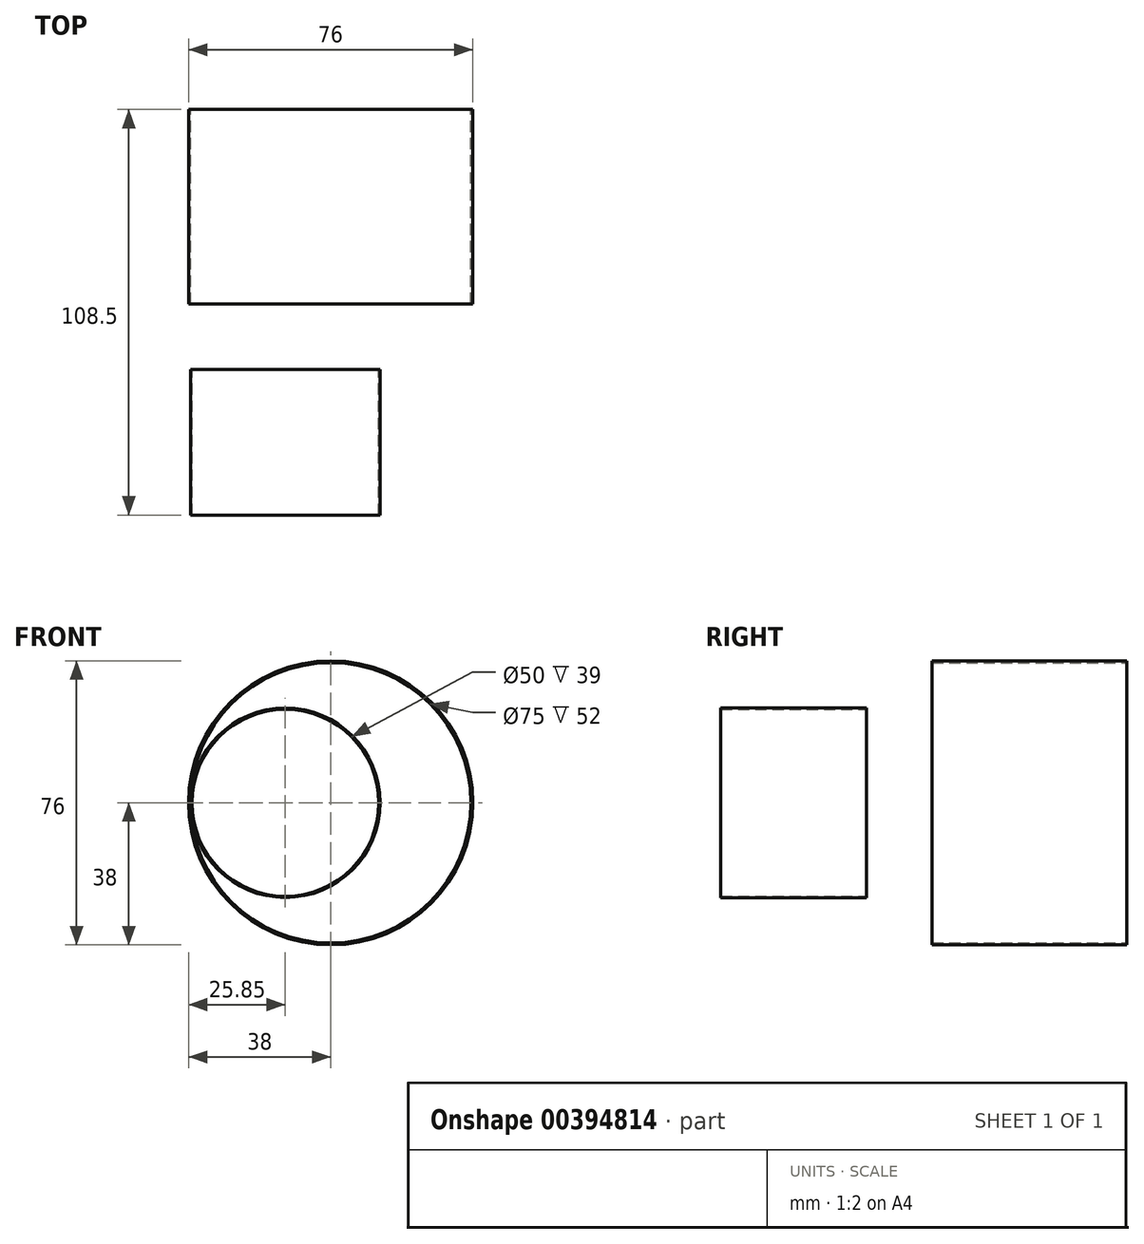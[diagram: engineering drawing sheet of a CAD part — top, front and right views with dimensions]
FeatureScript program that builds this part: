
annotation { "Feature Type Name" : "Feature", "Feature Type Description" : "" }
export const myFeature = defineFeature(function(context is Context, id is Id, definition is map)
    precondition{}
    {
        {
            var Q0;
            Q0=qCreatedBy(makeId("Front.planeOp"),FACE);
            var sketch = newSketch(context, id + "F0", { "sketchPlane" : qUnion([Q0])});
            skCircle(sketch, "E0", {"center": v(0, 0) * mm, "radius": 38 * mm});
            skCircle(sketch, "E1", {"center": v(0, 0) * mm, "radius": 37.5 * mm});
            skSolve(sketch);
        }
        {
            var Q0;
            Q0=makeQuery(id+"F0.imprint","IMPRINT",FACE,{"disambiguationData":[TD([[makeQuery(id+"F0.imprint","IMPRINT",EDGE,{"derivedFrom":sQuery(id+"F0.wireOp",EDGE,"E0")}),1.0]])]});
            extrude(context, id + "F1", {"entities" : qUnion([Q0]), "depth" : 52 * mm});
        }
        {
            var Q0;
            Q0=qCreatedBy(makeId("Front.planeOp"),FACE);
            cPlane(context, id + "F2", {"entities" : qUnion([Q0]), "cplaneType" : CPlaneType.OFFSET, "offset" : 69.5 * mm, "width" : 152.4 * mm, "height" : 152.4 * mm});
        }
        {
            var Q0;
            Q0=qCreatedBy(id+"F2.planeOp",FACE);
            var sketch = newSketch(context, id + "F3", { "sketchPlane" : qUnion([Q0])});
            skCircle(sketch, "E2", {"center": v(-12.15, 0) * mm, "radius": 25.35 * mm});
            skCircle(sketch, "E3", {"center": v(-12.15, 0) * mm, "radius": 25 * mm});
            skSolve(sketch);
        }
        {
            var Q0;
            Q0=makeQuery(id+"F3.imprint","IMPRINT",FACE,{"disambiguationData":[TD([[makeQuery(id+"F3.imprint","IMPRINT",EDGE,{"derivedFrom":sQuery(id+"F3.wireOp",EDGE,"E2")}),1.0]])]});
            extrude(context, id + "F4", {"entities" : qUnion([Q0]), "depth" : 39 * mm});
        }
        {
            var Q0;
            Q0=makeQuery(id+"F1.opExtrude","CAP_FACE",FACE,{"disambiguationData":[OSD([sQuery(id+"F0.wireOp",EDGE,"E0"),sQuery(id+"F0.wireOp",EDGE,"E1")])],"isStart":false});
            var Q1;
            Q1=makeQuery(id+"F1.opExtrude","CAP_EDGE",EDGE,{"disambiguationData":[OSD([sQuery(id+"F0.wireOp",EDGE,"E1")])],"isStart":false});
            var Q2;
            Q2=makeQuery(id+"F4.opExtrude","CAP_EDGE",EDGE,{"disambiguationData":[OSD([sQuery(id+"F3.wireOp",EDGE,"E2")])],"isStart":true});
            loft(context, id + "F5", {"bodyType" : ToolBodyType.SURFACE, "sheetProfilesArray" : [{ "sheetProfileEntities" : qUnion([Q0]) }], "wireProfilesArray" : [{ "wireProfileEntities" : qUnion([Q1]) }, { "wireProfileEntities" : qUnion([Q2]) }]});
        }
    });
